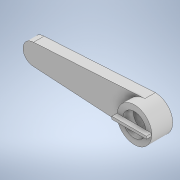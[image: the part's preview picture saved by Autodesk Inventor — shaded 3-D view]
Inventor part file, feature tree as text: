
AUTODESK INVENTOR PART (.ipt)
format: ipt  version: 2021 (Build 250183000, 183)  size: 130,048 bytes
history: native  units: mm
features: extrude x3, sketch x3
ambient origin geometry x8: Origin, YZ Plane, XZ Plane, XY Plane, X Axis, Y Axis, Z Axis, Center Point
bodies: Solid1 (feature_tree)
feature tree (6):
  extrude  "Extrusion1"  Depth=4.0mm
  extrude  "Extrusion2"  Depth=2.0mm TaperAngle=0.0deg
  extrude  "Extrusion3"  Depth=2.0mm TaperAngle=0.0deg
  sketch  "Sketch1"  dims[d0=6.6mm d1=4.0mm]
  sketch  "Sketch2"  dims[d2=21.2mm d3=2.0mm d4=0.0mm]
  sketch  "Sketch3"  dims[d5=4.4mm d6=2.0mm d7=0.0mm d8=0.25mm d9=0.25mm d10=1.0mm d11=0.0mm]
